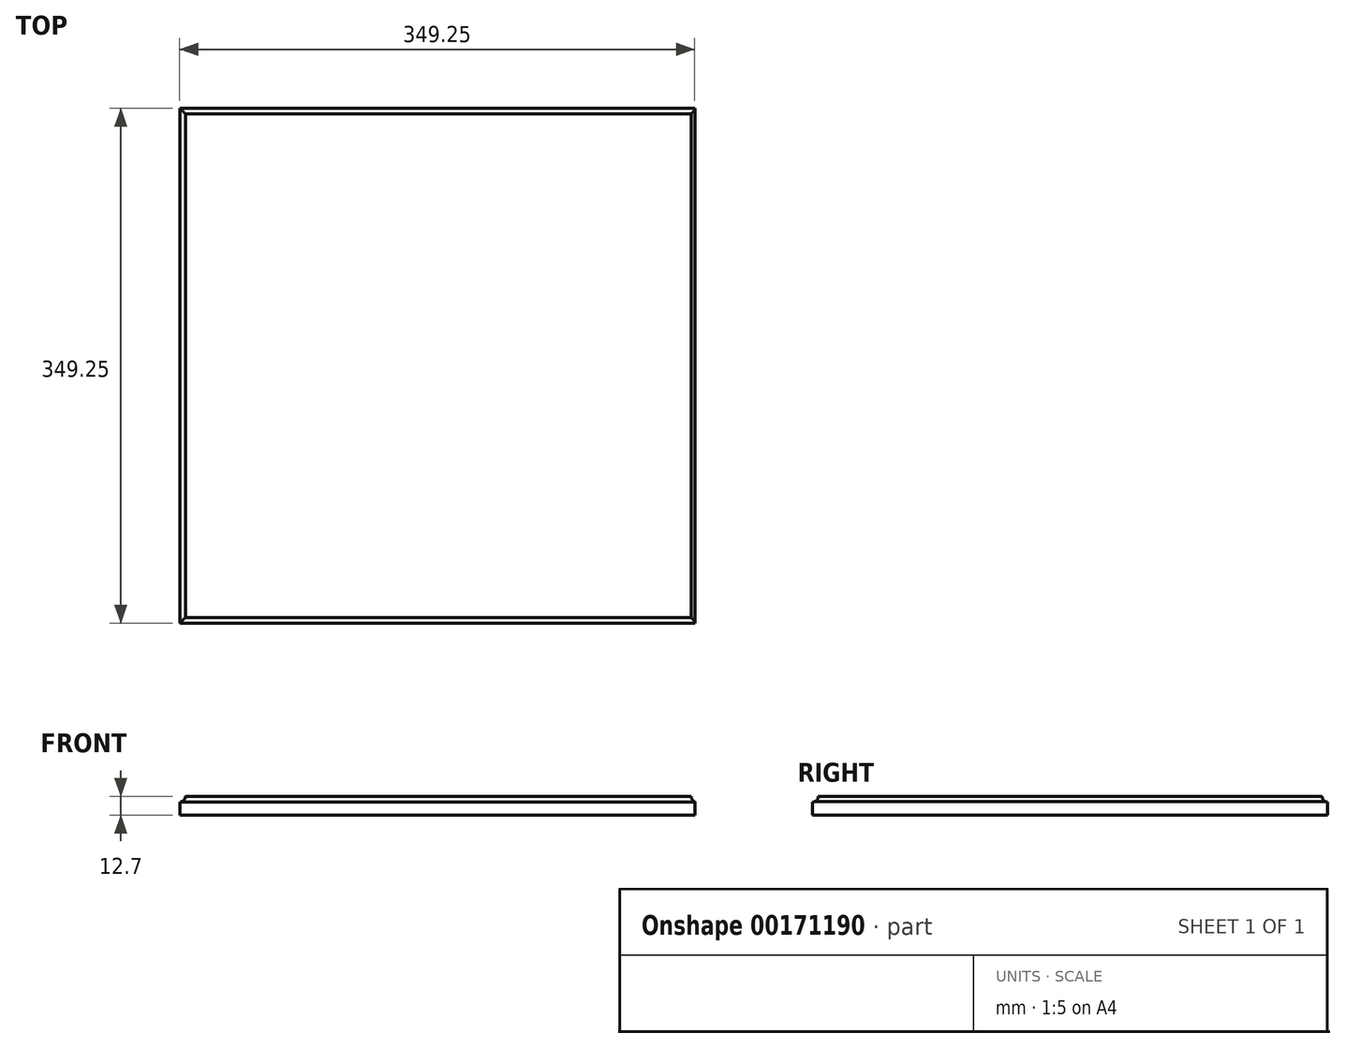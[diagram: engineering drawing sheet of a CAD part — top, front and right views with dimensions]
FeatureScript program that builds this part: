
annotation { "Feature Type Name" : "Feature", "Feature Type Description" : "" }
export const myFeature = defineFeature(function(context is Context, id is Id, definition is map)
    precondition{}
    {
        {
            var Q0;
            Q0=qCreatedBy(makeId("Top.planeOp"),FACE);
            var sketch = newSketch(context, id + "F0", { "sketchPlane" : qUnion([Q0])});
            skLineSegment(sketch, "E0.bottom", {"start": v(-191.63, 239.2) * mm, "end": v(157.62, 239.2) * mm});
            skLineSegment(sketch, "E0.top", {"start": v(-191.63, -110.05) * mm, "end": v(157.62, -110.05) * mm});
            skLineSegment(sketch, "E0.left", {"start": v(-191.63, 239.2) * mm, "end": v(-191.63, -110.05) * mm});
            skLineSegment(sketch, "E0.right", {"start": v(157.62, 239.2) * mm, "end": v(157.62, -110.05) * mm});
            skSolve(sketch);
        }
        {
            var Q0;
            Q0=makeQuery(id+"F0.imprint","IMPRINT",FACE,{"disambiguationData":[TD([[makeQuery(id+"F0.imprint","IMPRINT",EDGE,{"derivedFrom":sQuery(id+"F0.wireOp",EDGE,"E0.bottom")}),-1.0]])]});
            extrude(context, id + "F1", {"entities" : qUnion([Q0]), "depth" : 12.7 * mm});
        }
        {
            var Q0;
            Q0=makeQuery(id+"F1.opExtrude","SWEPT_FACE",FACE,{"disambiguationData":[OSD([sQuery(id+"F0.wireOp",EDGE,"E0.top")])]});
            var sketch = newSketch(context, id + "F2", { "sketchPlane" : qUnion([Q0])});
            skCircle(sketch, "E1", {"center": v(-191.63, 12.7) * mm, "radius": 3.81 * mm});
            skSolve(sketch);
        }
        {
            var Q0;
            Q0=makeQuery(id+"F1.opExtrude","SWEPT_FACE",FACE,{"disambiguationData":[OSD([sQuery(id+"F0.wireOp",EDGE,"E0.left")])]});
            var sketch = newSketch(context, id + "F3", { "sketchPlane" : qUnion([Q0])});
            skCircle(sketch, "E2", {"center": v(110.05, 12.7) * mm, "radius": 3.81 * mm});
            skCircle(sketch, "E3", {"center": v(-239.2, 12.7) * mm, "radius": 3.81 * mm});
            skSolve(sketch);
        }
        {
            var Q0;
            {var subQ0=sQuery(id+"F3.wireOp",EDGE,"E2");var subQ1=sQuery(id+"F0.wireOp",EDGE,"E0.left");var subQ4=makeQuery(id+"F1.opExtrude","CAP_EDGE",EDGE,{"disambiguationData":[OSD([subQ1])],"isStart":false});var subQ5=makeQuery(id+"F3.imprint","INTERSECT",VERTEX,{"derivedFrom":[subQ4,subQ0]});Q0=makeQuery(id+"F3.imprint","IMPRINT",FACE,{"disambiguationData":[TD([[makeQuery(id+"F3.imprint","IMPRINT",EDGE,{"disambiguationData":[TD([[subQ5,1.0]])],"derivedFrom":subQ0}),1.0]])]});}
            extrude(context, id + "F4", {"entities" : qUnion([Q0]), "operationType" : NewBodyOperationType.REMOVE, "endBound" : BoundingType.THROUGH_ALL, "oppositeDirection" : true, "depth" : 381 * mm});
        }
        {
            var Q0;
            {var subQ0=sQuery(id+"F2.wireOp",EDGE,"E1");var subQ1=sQuery(id+"F0.wireOp",EDGE,"E0.top");var subQ4=makeQuery(id+"F1.opExtrude","CAP_EDGE",EDGE,{"disambiguationData":[OSD([subQ1])],"isStart":false});var subQ5=makeQuery(id+"F2.imprint","INTERSECT",VERTEX,{"derivedFrom":[subQ4,subQ0]});Q0=makeQuery(id+"F2.imprint","IMPRINT",FACE,{"disambiguationData":[TD([[makeQuery(id+"F2.imprint","IMPRINT",EDGE,{"disambiguationData":[TD([[subQ5,-1.0]])],"derivedFrom":subQ0}),1.0]])]});}
            var Q1;
            Q1=sQuery(id+"F2.wireOp",EDGE,"E1");
            extrude(context, id + "F5", {"entities" : qUnion([Q0]), "operationType" : NewBodyOperationType.REMOVE, "surfaceEntities" : qUnion([Q1]), "endBound" : BoundingType.THROUGH_ALL, "oppositeDirection" : true, "depth" : 25.4 * mm});
        }
        {
            var Q0;
            Q0 = qSketchRegion(id + "F3", true);
            extrude(context, id + "F6", {"entities" : qUnion([Q0]), "operationType" : NewBodyOperationType.REMOVE, "endBound" : BoundingType.THROUGH_ALL, "oppositeDirection" : true, "depth" : 25.4 * mm});
        }
        {
            var Q0;
            Q0 = qSketchRegion(id + "F2", true);
            extrude(context, id + "F7", {"entities" : qUnion([Q0]), "operationType" : NewBodyOperationType.REMOVE, "endBound" : BoundingType.THROUGH_ALL, "oppositeDirection" : true, "depth" : 25.4 * mm});
        }
        {
            var Q0;
            {var subQ0=sQuery(id+"F0.wireOp",EDGE,"E0.top");var subQ1=makeQuery(id+"F1.opExtrude","CAP_EDGE",EDGE,{"disambiguationData":[OSD([subQ0])],"isStart":true});Q0=makeQuery(id+"F2.imprint","IMPRINT",FACE,{"disambiguationData":[TD([[makeQuery(id+"F2.imprint","IMPRINT",EDGE,{"derivedFrom":subQ1}),1.0]])]});}
            var sketch = newSketch(context, id + "F8", { "sketchPlane" : qUnion([Q0])});
            skCircle(sketch, "E4", {"center": v(189.4, 12.57) * mm, "radius": 3.81 * mm});
            skSolve(sketch);
        }
        {
            var Q0;
            Q0 = qSketchRegion(id + "F8", true);
            extrude(context, id + "F9", {"entities" : qUnion([Q0]), "operationType" : NewBodyOperationType.REMOVE, "endBound" : BoundingType.THROUGH_ALL, "oppositeDirection" : true, "depth" : 25.4 * mm});
        }
        {
            var Q0;
            {var subQ0=sQuery(id+"F0.wireOp",EDGE,"E0.top");var subQ1=makeQuery(id+"F1.opExtrude","CAP_EDGE",EDGE,{"disambiguationData":[OSD([subQ0])],"isStart":true});Q0=makeQuery(id+"F2.imprint","IMPRINT",FACE,{"disambiguationData":[TD([[makeQuery(id+"F2.imprint","IMPRINT",EDGE,{"derivedFrom":subQ1}),1.0]])]});}
            var sketch = newSketch(context, id + "F10", { "sketchPlane" : qUnion([Q0])});
            skCircle(sketch, "E5", {"center": v(159.06, 12.64) * mm, "radius": 3.8 * mm});
            skSolve(sketch);
        }
        {
            var Q0;
            Q0 = qSketchRegion(id + "F10", true);
            extrude(context, id + "F11", {"entities" : qUnion([Q0]), "operationType" : NewBodyOperationType.REMOVE, "endBound" : BoundingType.THROUGH_ALL, "oppositeDirection" : true, "depth" : 25.4 * mm});
        }
    });
